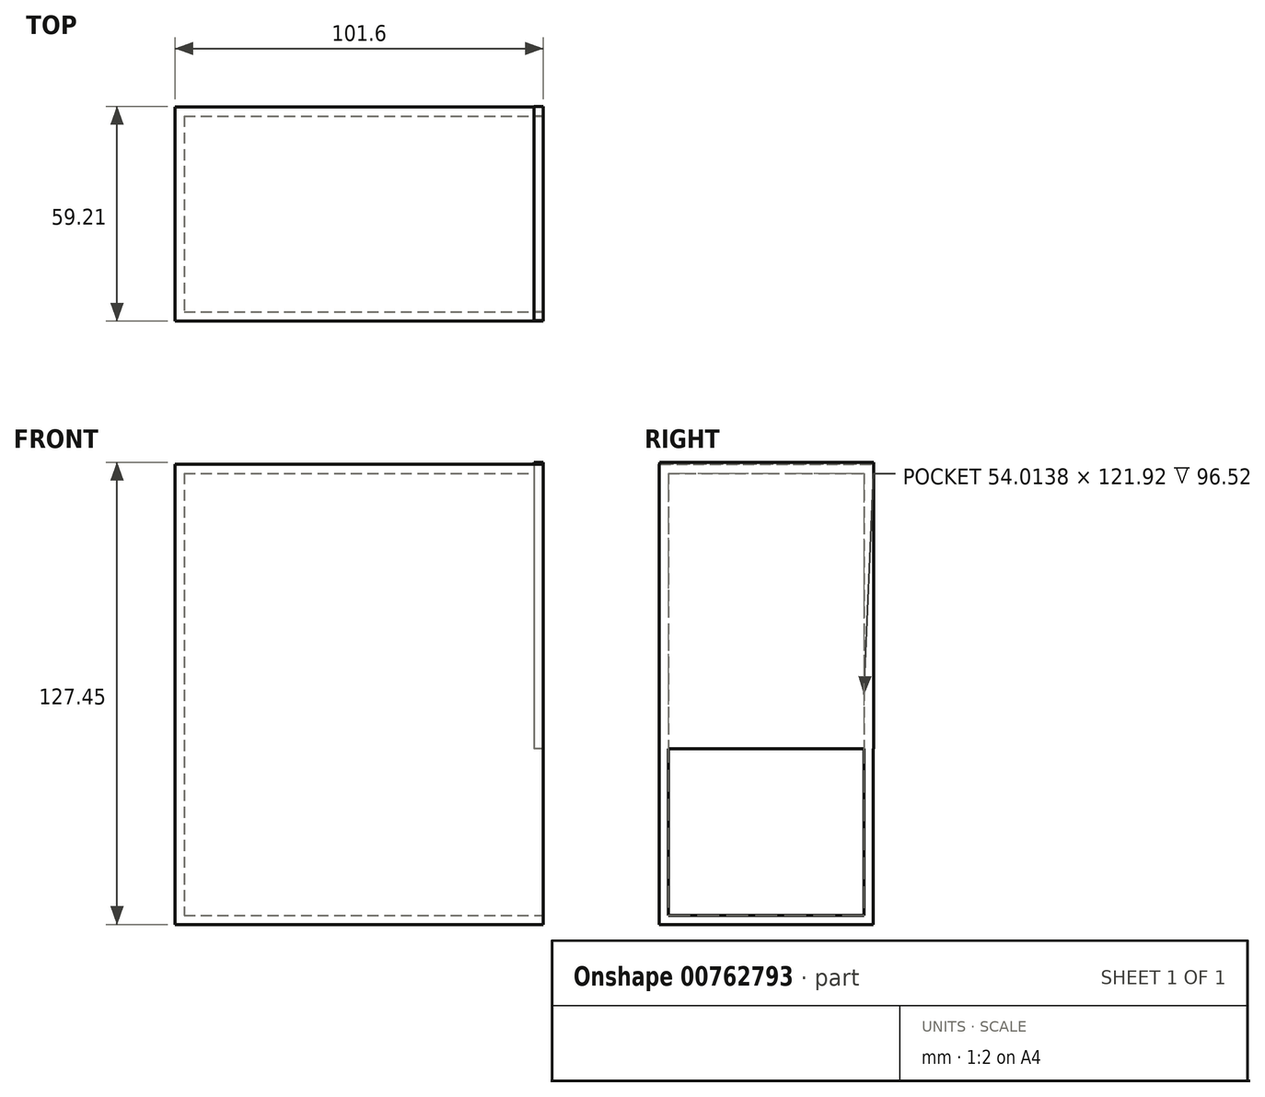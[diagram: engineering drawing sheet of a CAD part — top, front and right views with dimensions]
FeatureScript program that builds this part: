
annotation { "Feature Type Name" : "Feature", "Feature Type Description" : "" }
export const myFeature = defineFeature(function(context is Context, id is Id, definition is map)
    precondition{}
    {
        {
            var Q0;
            Q0=qCreatedBy(makeId("Top.planeOp"),FACE);
            var sketch = newSketch(context, id + "F0", { "sketchPlane" : qUnion([Q0])});
            skLineSegment(sketch, "E0.bottom", {"start": v(-52.38, 26.83) * mm, "end": v(49.22, 26.83) * mm});
            skLineSegment(sketch, "E0.top", {"start": v(-52.38, -32.26) * mm, "end": v(49.22, -32.26) * mm});
            skLineSegment(sketch, "E0.left", {"start": v(-52.38, 26.83) * mm, "end": v(-52.38, -32.26) * mm});
            skLineSegment(sketch, "E0.right", {"start": v(49.22, 26.83) * mm, "end": v(49.22, -32.26) * mm});
            skSolve(sketch);
        }
        {
            var Q0;
            Q0=makeQuery(id+"F0.imprint","IMPRINT",FACE,{"disambiguationData":[TD([[makeQuery(id+"F0.imprint","IMPRINT",EDGE,{"derivedFrom":sQuery(id+"F0.wireOp",EDGE,"E0.bottom")}),-1.0]])]});
            extrude(context, id + "F1", {"entities" : qUnion([Q0]), "depth" : 127 * mm, "offsetDistance" : 25.4 * mm});
        }
        {
            var Q0;
            Q0=makeQuery(id+"F1.opExtrude","SWEPT_FACE",FACE,{"disambiguationData":[OSD([sQuery(id+"F0.wireOp",EDGE,"E0.right")])]});
            var Q1;
            Q1=makeQuery(id+"F1.opExtrude","SWEPT_BODY",BODY,{"disambiguationData":[OSD([sQuery(id+"F0.wireOp",EDGE,"E0.bottom"),sQuery(id+"F0.wireOp",EDGE,"E0.top"),sQuery(id+"F0.wireOp",EDGE,"E0.left"),sQuery(id+"F0.wireOp",EDGE,"E0.right")])]});
            shell(context, id + "F2", {"entities" : qUnion([Q0]), "parts" : qUnion([Q1]), "thickness" : 2.54 * mm});
        }
        {
            var Q0;
            Q0=makeQuery(id+"F1.opExtrude","SWEPT_FACE",FACE,{"disambiguationData":[OSD([sQuery(id+"F0.wireOp",EDGE,"E0.right")])]});
            cPlane(context, id + "F3", {"entities" : qUnion([Q0]), "cplaneType" : CPlaneType.OFFSET, "offset" : 0 * mm, "width" : 152.4 * mm, "height" : 152.4 * mm});
        }
        {
            var Q0;
            Q0=qCreatedBy(id+"F3.planeOp",FACE);
            var sketch = newSketch(context, id + "F4", { "sketchPlane" : qUnion([Q0])});
            skLineSegment(sketch, "E1.bottom", {"start": v(-32.08, 127.45) * mm, "end": v(26.95, 127.45) * mm});
            skLineSegment(sketch, "E1.top", {"start": v(-32.08, 48.44) * mm, "end": v(26.95, 48.44) * mm});
            skLineSegment(sketch, "E1.left", {"start": v(-32.08, 127.45) * mm, "end": v(-32.08, 48.44) * mm});
            skLineSegment(sketch, "E1.right", {"start": v(26.95, 127.45) * mm, "end": v(26.95, 48.44) * mm});
            skSolve(sketch);
        }
        {
            var Q0;
            Q0=makeQuery(id+"F4.imprint","IMPRINT",FACE,{"disambiguationData":[TD([[makeQuery(id+"F4.imprint","IMPRINT",EDGE,{"derivedFrom":sQuery(id+"F4.wireOp",EDGE,"E1.bottom")}),-1.0]])]});
            extrude(context, id + "F5", {"entities" : qUnion([Q0]), "operationType" : NewBodyOperationType.ADD, "oppositeDirection" : true, "depth" : 2.54 * mm, "offsetDistance" : 25.4 * mm});
        }
    });
